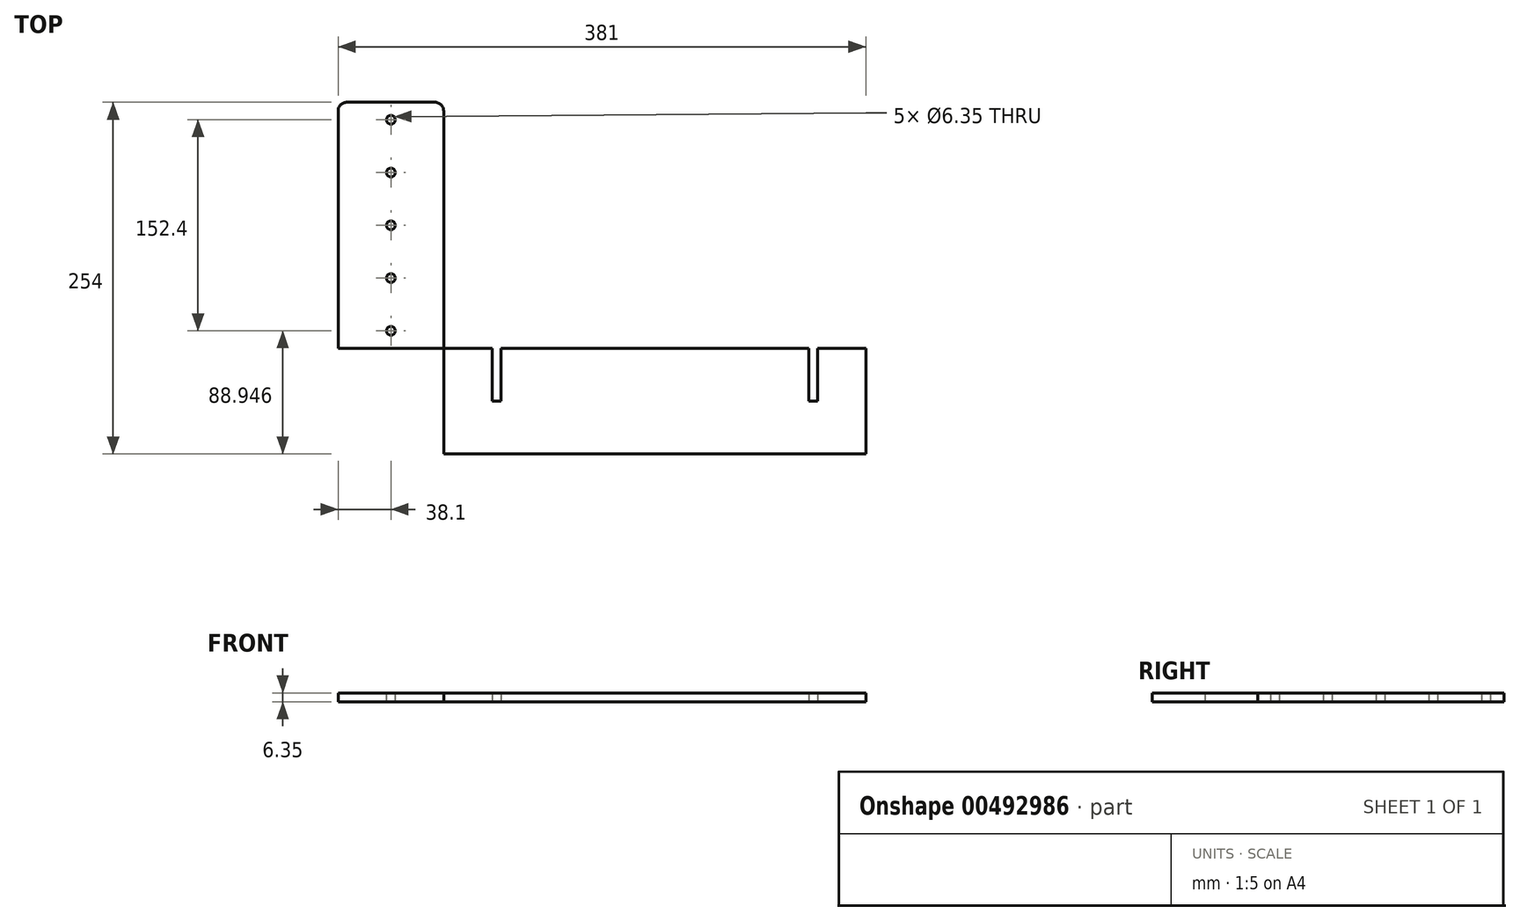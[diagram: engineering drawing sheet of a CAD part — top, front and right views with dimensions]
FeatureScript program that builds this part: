
annotation { "Feature Type Name" : "Feature", "Feature Type Description" : "" }
export const myFeature = defineFeature(function(context is Context, id is Id, definition is map)
    precondition{}
    {
        {
            var Q0;
            Q0=qCreatedBy(makeId("Top.planeOp"),FACE);
            var sketch = newSketch(context, id + "F0", { "sketchPlane" : qUnion([Q0])});
            skLineSegment(sketch, "E0.bottom", {"start": v(0, 0) * mm, "end": v(381, 0) * mm});
            skLineSegment(sketch, "E0.top", {"start": v(0, -76.2) * mm, "end": v(381, -76.2) * mm});
            skLineSegment(sketch, "E0.left", {"start": v(0, 0) * mm, "end": v(0, -76.2) * mm});
            skLineSegment(sketch, "E0.right", {"start": v(381, 0) * mm, "end": v(381, -76.2) * mm});
            skLineSegment(sketch, "E1.bottom", {"start": v(0, -76.2) * mm, "end": v(76.2, -76.2) * mm});
            skLineSegment(sketch, "E1.top", {"start": v(6.35, 177.8) * mm, "end": v(69.85, 177.8) * mm});
            skLineSegment(sketch, "E1.left", {"start": v(0, -76.2) * mm, "end": v(0, 171.45) * mm});
            skLineSegment(sketch, "E1.right", {"start": v(76.2, -76.2) * mm, "end": v(76.2, 171.45) * mm});
            skLineSegment(sketch, "E2.bottom", {"start": v(250.83, 0) * mm, "end": v(257.18, 0) * mm});
            skLineSegment(sketch, "E2.top", {"start": v(250.83, -76.2) * mm, "end": v(257.18, -76.2) * mm});
            skLineSegment(sketch, "E3.bottom", {"start": v(257.18, -76.2) * mm, "end": v(250.83, -76.2) * mm});
            skLineSegment(sketch, "E4.bottom", {"start": v(111.13, 0) * mm, "end": v(117.48, 0) * mm});
            skLineSegment(sketch, "E4.top", {"start": v(111.13, -38.1) * mm, "end": v(117.48, -38.1) * mm});
            skLineSegment(sketch, "E4.left", {"start": v(111.13, 0) * mm, "end": v(111.13, -38.1) * mm});
            skLineSegment(sketch, "E4.right", {"start": v(117.48, 0) * mm, "end": v(117.48, -38.1) * mm});
            skLineSegment(sketch, "E5.bottom", {"start": v(339.73, 0) * mm, "end": v(346.08, 0) * mm});
            skLineSegment(sketch, "E5.top", {"start": v(339.73, -38.1) * mm, "end": v(346.08, -38.1) * mm});
            skLineSegment(sketch, "E5.left", {"start": v(339.73, 0) * mm, "end": v(339.73, -38.1) * mm});
            skLineSegment(sketch, "E5.right", {"start": v(346.08, 0) * mm, "end": v(346.08, -38.1) * mm});
            skLineSegment(sketch, "E6", {"start": v(114.3, -38.1) * mm, "end": v(114.3, 0) * mm});
            skLineSegment(sketch, "E7", {"start": v(342.9, 0) * mm, "end": v(342.9, -38.1) * mm});
            skPoint(sketch, "E8.visualSharp", {"position": v(0, 177.8) * mm});
            skArc(sketch, "E8.filletArc", {"start": v(6.35, 177.8) * mm, "mid": v(1.86, 175.94) * mm, "end": v(0, 171.45) * mm});
            skPoint(sketch, "E9.visualSharp", {"position": v(76.2, 177.8) * mm});
            skArc(sketch, "E9.filletArc", {"start": v(76.2, 171.45) * mm, "mid": v(74.34, 175.94) * mm, "end": v(69.85, 177.8) * mm});
            skSolve(sketch);
        }
        {
            var Q0;
            {var subQ5=sQuery(id+"F0.wireOp",EDGE,"E1.top");Q0=makeQuery(id+"F0.imprint","IMPRINT",FACE,{"disambiguationData":[TD([[makeQuery(id+"F0.imprint","IMPRINT",EDGE,{"derivedFrom":subQ5}),-1.0]])]});}
            var Q1;
            {var subQ5=sQuery(id+"F0.wireOp",EDGE,"E1.bottom");Q1=makeQuery(id+"F0.imprint","IMPRINT",FACE,{"disambiguationData":[TD([[makeQuery(id+"F0.imprint","IMPRINT",EDGE,{"derivedFrom":subQ5}),1.0]])]});}
            var Q2;
            {var subQ0=sQuery(id+"F0.wireOp",EDGE,"E2.left");Q2=makeQuery(id+"F0.imprint","IMPRINT",FACE,{"disambiguationData":[TD([[makeQuery(id+"F0.imprint","IMPRINT",EDGE,{"derivedFrom":subQ0}),-1.0]])]});}
            var Q3;
            {var subQ1=sQuery(id+"F0.wireOp",EDGE,"E0.right");Q3=makeQuery(id+"F0.imprint","IMPRINT",FACE,{"disambiguationData":[TD([[makeQuery(id+"F0.imprint","IMPRINT",EDGE,{"derivedFrom":subQ1}),-1.0]])]});}
            var Q4;
            {var subQ0=sQuery(id+"F0.wireOp",EDGE,"E2.right");Q4=makeQuery(id+"F0.imprint","IMPRINT",FACE,{"disambiguationData":[TD([[makeQuery(id+"F0.imprint","IMPRINT",EDGE,{"derivedFrom":subQ0}),-1.0]])]});}
            var Q5;
            {var subQ0=sQuery(id+"F0.wireOp",EDGE,"E2.left");Q5=makeQuery(id+"F0.imprint","IMPRINT",FACE,{"disambiguationData":[TD([[makeQuery(id+"F0.imprint","IMPRINT",EDGE,{"derivedFrom":subQ0}),1.0]])]});}
            extrude(context, id + "F1", {"entities" : qUnion([Q0, Q1, Q2, Q3, Q4, Q5]), "depth" : 6.35 * mm});
        }
        {
            var Q0;
            Q0=makeQuery(id+"F1.opExtrude","CAP_FACE",FACE,{"disambiguationData":[OSD([sQuery(id+"F0.wireOp",EDGE,"E0.bottom"),sQuery(id+"F0.wireOp",EDGE,"E0.top"),sQuery(id+"F0.wireOp",EDGE,"E0.right"),sQuery(id+"F0.wireOp",EDGE,"E1.bottom"),sQuery(id+"F0.wireOp",EDGE,"E1.top"),sQuery(id+"F0.wireOp",EDGE,"E1.left"),sQuery(id+"F0.wireOp",EDGE,"E1.right"),sQuery(id+"F0.wireOp",EDGE,"E2.bottom"),sQuery(id+"F0.wireOp",EDGE,"E3.top"),sQuery(id+"F0.wireOp",EDGE,"E3.left"),sQuery(id+"F0.wireOp",EDGE,"E3.right")])],"isStart":false});
            var sketch = newSketch(context, id + "F2", { "sketchPlane" : qUnion([Q0])});
            skLineSegment(sketch, "E10.0.0", {"start": v(0, -76.2) * mm, "end": v(0, -76.2) * mm});
            skLineSegment(sketch, "E10.0.1", {"start": v(0, -76.2) * mm, "end": v(381, -76.2) * mm});
            skLineSegment(sketch, "E10.0.2", {"start": v(381, -76.2) * mm, "end": v(381, -38.1) * mm});
            skLineSegment(sketch, "E10.0.3", {"start": v(257.18, -38.1) * mm, "end": v(381, -38.1) * mm});
            skLineSegment(sketch, "E10.0.4", {"start": v(257.18, -38.1) * mm, "end": v(257.18, -76.2) * mm});
            skLineSegment(sketch, "E10.0.5", {"start": v(257.18, -76.2) * mm, "end": v(381, -76.2) * mm});
            skLineSegment(sketch, "E10.0.6", {"start": v(381, -76.2) * mm, "end": v(381, 0) * mm});
            skLineSegment(sketch, "E10.0.7", {"start": v(381, 0) * mm, "end": v(117.48, 0) * mm});
            skLineSegment(sketch, "E10.0.8", {"start": v(76.2, 0) * mm, "end": v(76.2, 171.45) * mm});
            skLineSegment(sketch, "E10.0.9", {"start": v(76.2, 177.8) * mm, "end": v(0, 177.8) * mm});
            skCircle(sketch, "E11", {"center": v(38.1, 127.05) * mm, "radius": 3.18 * mm});
            skPoint(sketch, "E11.centerSnap0", {"position": v(38.1, 177.8) * mm});
            skCircle(sketch, "E12", {"center": v(38.1, 88.95) * mm, "radius": 3.18 * mm});
            skCircle(sketch, "E13", {"center": v(38.1, 50.85) * mm, "radius": 3.18 * mm});
            skCircle(sketch, "E14", {"center": v(38.1, 12.75) * mm, "radius": 3.18 * mm});
            skCircle(sketch, "E15", {"center": v(38.1, 165.15) * mm, "radius": 3.18 * mm});
            skSolve(sketch);
        }
        {
            var Q0;
            Q0=makeQuery(id+"F2.imprint","IMPRINT",FACE,{"disambiguationData":[TD([[makeQuery(id+"F2.imprint","IMPRINT",EDGE,{"derivedFrom":sQuery(id+"F2.wireOp",EDGE,"E14")}),1.0]])]});
            var Q1;
            Q1=makeQuery(id+"F2.imprint","IMPRINT",FACE,{"disambiguationData":[TD([[makeQuery(id+"F2.imprint","IMPRINT",EDGE,{"derivedFrom":sQuery(id+"F2.wireOp",EDGE,"E13")}),1.0]])]});
            var Q2;
            Q2=makeQuery(id+"F2.imprint","IMPRINT",FACE,{"disambiguationData":[TD([[makeQuery(id+"F2.imprint","IMPRINT",EDGE,{"derivedFrom":sQuery(id+"F2.wireOp",EDGE,"E12")}),1.0]])]});
            var Q3;
            Q3=makeQuery(id+"F2.imprint","IMPRINT",FACE,{"disambiguationData":[TD([[makeQuery(id+"F2.imprint","IMPRINT",EDGE,{"derivedFrom":sQuery(id+"F2.wireOp",EDGE,"E11")}),1.0]])]});
            var Q4;
            Q4=makeQuery(id+"F2.imprint","IMPRINT",FACE,{"disambiguationData":[TD([[makeQuery(id+"F2.imprint","IMPRINT",EDGE,{"derivedFrom":sQuery(id+"F2.wireOp",EDGE,"E15")}),1.0]])]});
            extrude(context, id + "F3", {"entities" : qUnion([Q0, Q1, Q2, Q3, Q4]), "operationType" : NewBodyOperationType.REMOVE, "oppositeDirection" : true, "depth" : 25.4 * mm});
        }
    });
